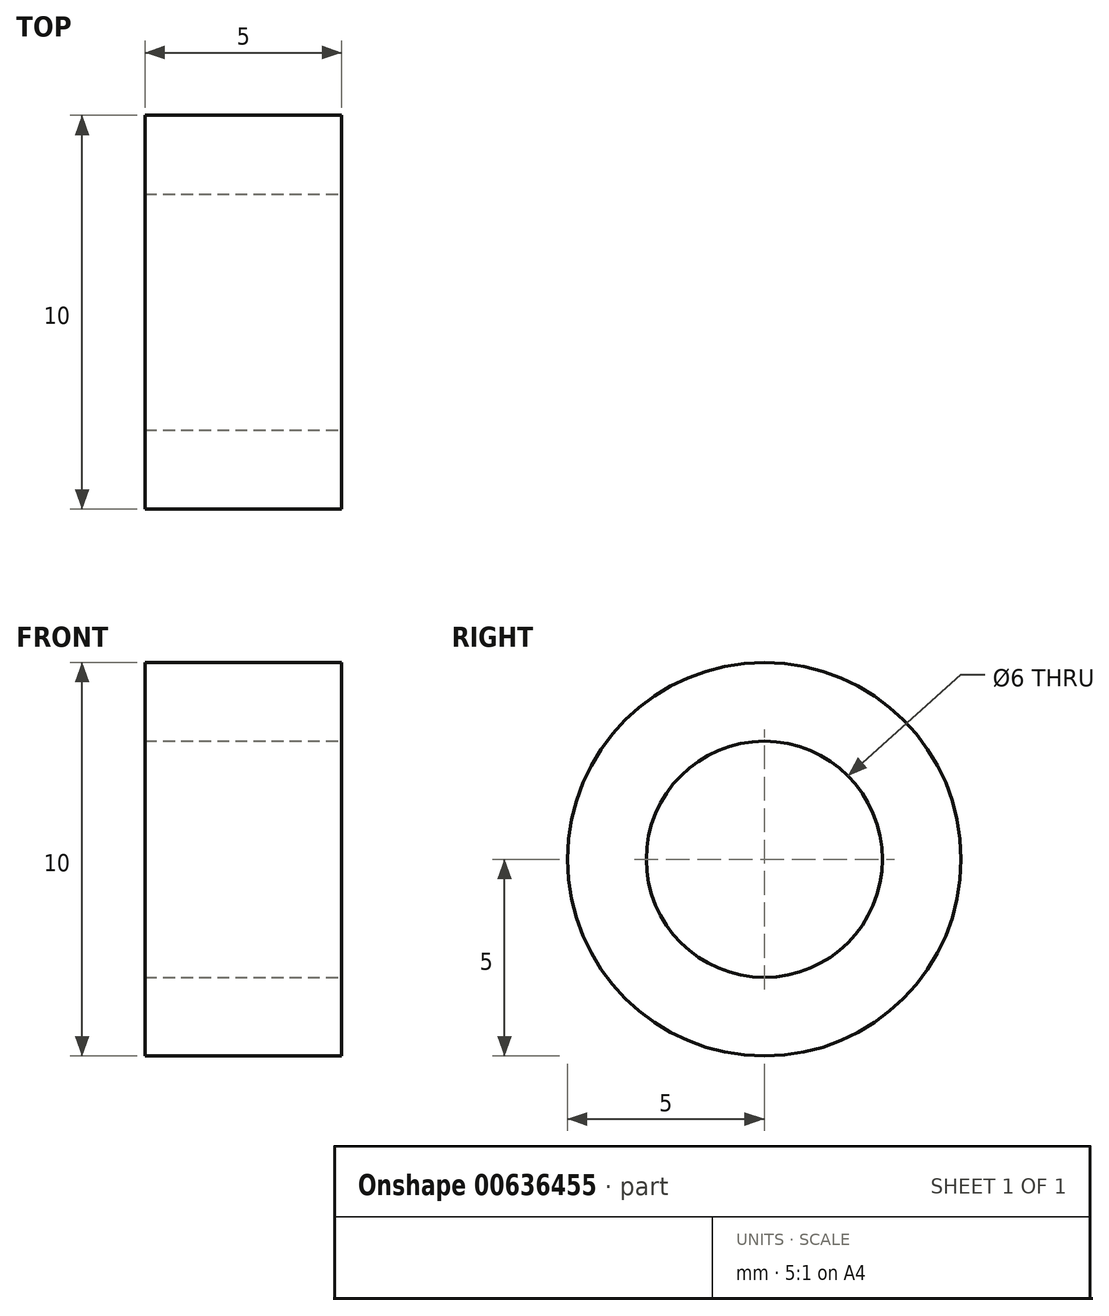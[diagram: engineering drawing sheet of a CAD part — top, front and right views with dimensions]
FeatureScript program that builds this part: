
annotation { "Feature Type Name" : "Feature", "Feature Type Description" : "" }
export const myFeature = defineFeature(function(context is Context, id is Id, definition is map)
    precondition{}
    {
        {
            var Q0;
            Q0=qCreatedBy(makeId("Right.planeOp"),FACE);
            var sketch = newSketch(context, id + "F0", { "sketchPlane" : qUnion([Q0])});
            skCircle(sketch, "E0", {"center": v(0, 0) * mm, "radius": 5 * mm});
            skCircle(sketch, "E1", {"center": v(0, 0) * mm, "radius": 3 * mm});
            skSolve(sketch);
        }
        {
            var Q0;
            Q0 = qSketchRegion(id + "F0", true);
            extrude(context, id + "F1", {"entities" : qUnion([Q0]), "oppositeDirection" : true, "depth" : 5 * mm, "offsetDistance" : 25 * mm});
        }
    });
